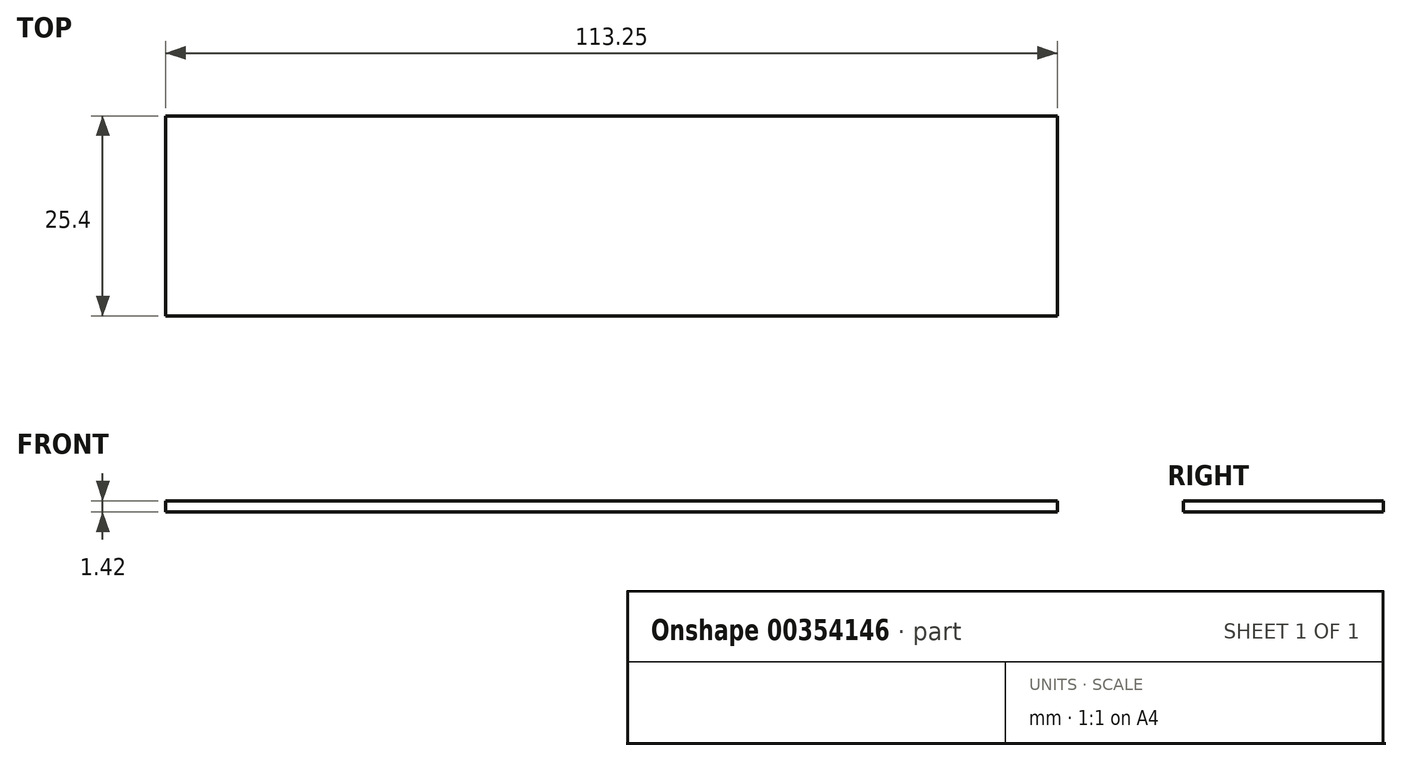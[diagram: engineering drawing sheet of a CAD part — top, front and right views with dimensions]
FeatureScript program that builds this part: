
annotation { "Feature Type Name" : "Feature", "Feature Type Description" : "" }
export const myFeature = defineFeature(function(context is Context, id is Id, definition is map)
    precondition{}
    {
        {
            var Q0;
            Q0=qCreatedBy(makeId("Front.planeOp"),FACE);
            var sketch = newSketch(context, id + "F0", { "sketchPlane" : qUnion([Q0])});
            skLineSegment(sketch, "E0.bottom", {"start": v(-53.63, 11.27) * mm, "end": v(59.62, 11.27) * mm});
            skLineSegment(sketch, "E0.top", {"start": v(-53.63, 12.7) * mm, "end": v(59.62, 12.7) * mm});
            skLineSegment(sketch, "E0.left", {"start": v(-53.63, 11.27) * mm, "end": v(-53.63, 12.7) * mm});
            skLineSegment(sketch, "E0.right", {"start": v(59.62, 11.27) * mm, "end": v(59.62, 12.7) * mm});
            skSolve(sketch);
        }
        {
            var Q0;
            Q0 = qSketchRegion(id + "F0", true);
            extrude(context, id + "F1", {"entities" : qUnion([Q0]), "depth" : 25.4 * mm});
        }
    });
